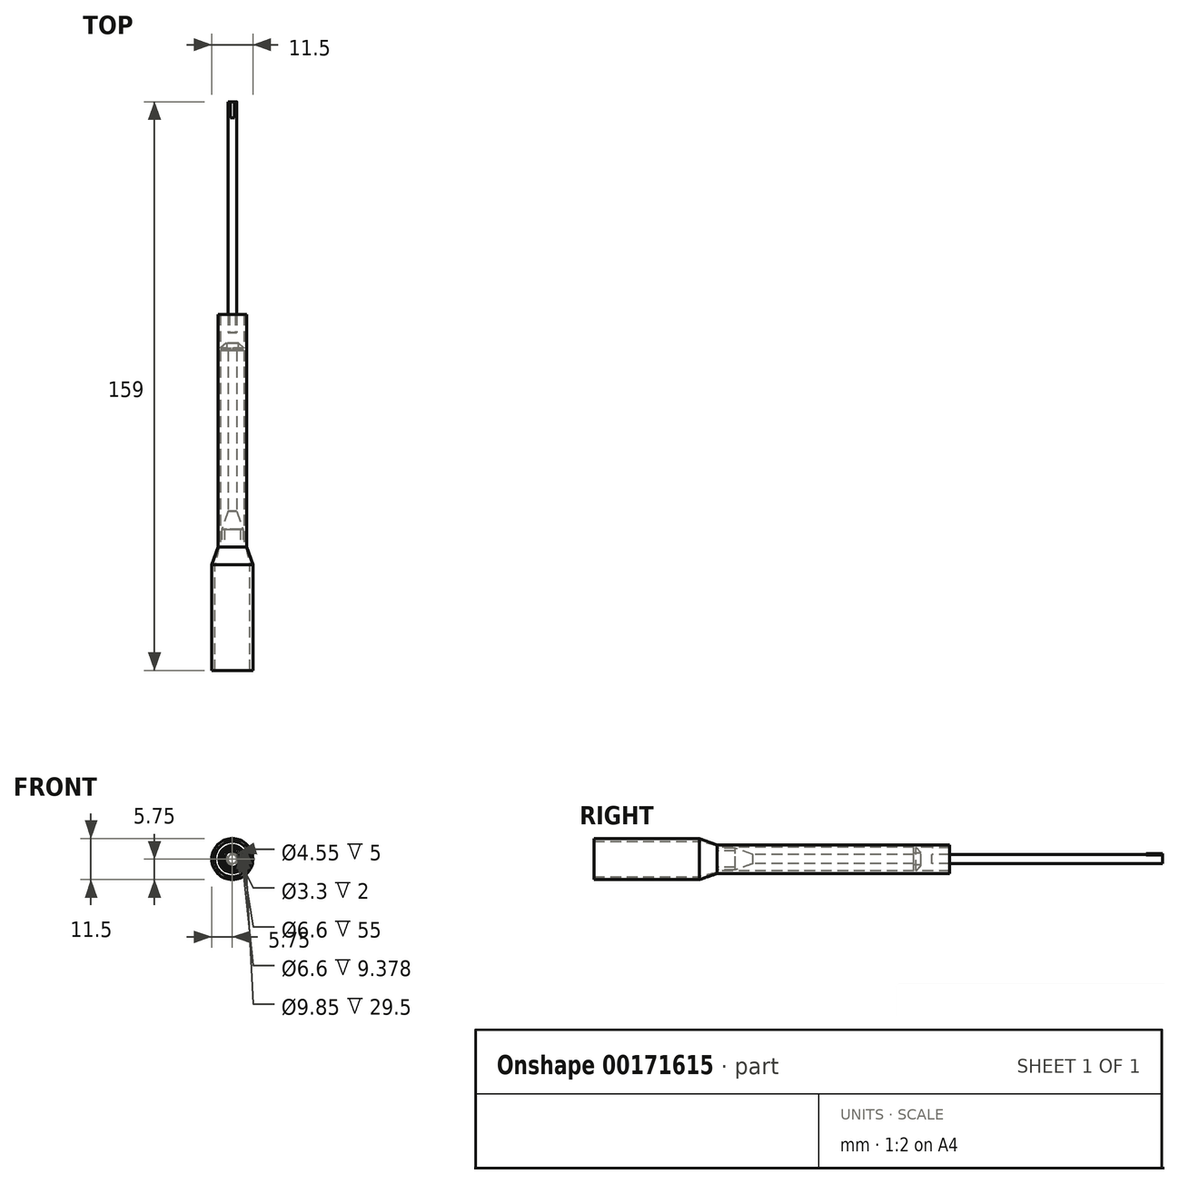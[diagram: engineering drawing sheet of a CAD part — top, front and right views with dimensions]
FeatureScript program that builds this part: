
annotation { "Feature Type Name" : "Feature", "Feature Type Description" : "" }
export const myFeature = defineFeature(function(context is Context, id is Id, definition is map)
    precondition{}
    {
        {
            var Q0;
            Q0=qCreatedBy(makeId("Front.planeOp"),FACE);
            var sketch = newSketch(context, id + "F0", { "sketchPlane" : qUnion([Q0])});
            skCircle(sketch, "E0", {"center": v(0, 0) * mm, "radius": 2.27 * mm});
            skCircle(sketch, "E1", {"center": v(0, 0) * mm, "radius": 3 * mm});
            skSolve(sketch);
        }
        {
            var Q0;
            Q0=makeQuery(id+"F0.imprint","IMPRINT",FACE,{"disambiguationData":[TD([[makeQuery(id+"F0.imprint","IMPRINT",EDGE,{"derivedFrom":sQuery(id+"F0.wireOp",EDGE,"E0")}),-1.0]])]});
            extrude(context, id + "F1", {"entities" : qUnion([Q0]), "oppositeDirection" : true, "depth" : 5 * mm});
        }
        {
            var Q0;
            Q0=qCreatedBy(makeId("Front.planeOp"),FACE);
            cPlane(context, id + "F2", {"entities" : qUnion([Q0]), "cplaneType" : CPlaneType.OFFSET, "offset" : 5 * mm, "oppositeDirection" : true, "width" : 150 * mm, "height" : 150 * mm});
        }
        {
            var Q0;
            Q0=qCreatedBy(id+"F2.planeOp",FACE);
            var sketch = newSketch(context, id + "F3", { "sketchPlane" : qUnion([Q0])});
            skCircle(sketch, "E2", {"center": v(0, 0) * mm, "radius": 3 * mm});
            skSolve(sketch);
        }
        {
            var Q0;
            Q0=qCreatedBy(id+"F2.planeOp",FACE);
            cPlane(context, id + "F4", {"entities" : qUnion([Q0]), "cplaneType" : CPlaneType.OFFSET, "offset" : 5 * mm, "oppositeDirection" : true, "width" : 150 * mm, "height" : 150 * mm});
        }
        {
            var Q0;
            Q0=qCreatedBy(id+"F4.planeOp",FACE);
            var sketch = newSketch(context, id + "F5", { "sketchPlane" : qUnion([Q0])});
            skCircle(sketch, "E3", {"center": v(0, 0) * mm, "radius": 1.25 * mm});
            skSolve(sketch);
        }
        {
            var Q1;
            Q1 = qSketchRegion(id + "F5", true);
            var Q2;
            Q2 = qSketchRegion(id + "F3", true);
            loft(context, id + "F6", {"operationType" : NewBodyOperationType.ADD, "sheetProfilesArray" : [{ "sheetProfileEntities" : qUnion([Q1]) }, { "sheetProfileEntities" : qUnion([Q2]) }]});
        }
        {
            var Q0;
            Q0 = qSketchRegion(id + "F5", true);
            extrude(context, id + "F7", {"entities" : qUnion([Q0]), "operationType" : NewBodyOperationType.ADD, "oppositeDirection" : true, "depth" : 110 * mm});
        }
        {
            var Q0;
            Q0=qCreatedBy(id+"F4.planeOp",FACE);
            cPlane(context, id + "F8", {"entities" : qUnion([Q0]), "cplaneType" : CPlaneType.OFFSET, "offset" : 110 * mm, "oppositeDirection" : true, "width" : 150 * mm, "height" : 150 * mm});
        }
        {
            var Q0;
            Q0=qCreatedBy(id+"F8.planeOp",FACE);
            var sketch = newSketch(context, id + "F9", { "sketchPlane" : qUnion([Q0])});
            skArc(sketch, "E4", {"start": v(-0.55, 1.12) * mm, "mid": v(0, -1.25) * mm, "end": v(0.55, 1.12) * mm});
            skLineSegment(sketch, "E5.bottom", {"start": v(-0.55, 1.5) * mm, "end": v(0.55, 1.5) * mm});
            skLineSegment(sketch, "E5.left", {"start": v(-0.55, 1.5) * mm, "end": v(-0.55, 1.12) * mm});
            skLineSegment(sketch, "E5.right", {"start": v(0.55, 1.5) * mm, "end": v(0.55, 1.12) * mm});
            skPoint(sketch, "E5.middle", {"position": v(0, 1.25) * mm});
            skPoint(sketch, "E6", {"position": v(-0.55, 1.12) * mm});
            skPoint(sketch, "E7", {"position": v(0.55, 1.12) * mm});
            skPoint(sketch, "E8.orphan", {"position": v(-0.55, 1) * mm});
            skPoint(sketch, "E9.orphan", {"position": v(0.55, 1) * mm});
            skSolve(sketch);
        }
        {
            var Q0;
            Q0=qCreatedBy(id+"F8.planeOp",FACE);
            cPlane(context, id + "F10", {"entities" : qUnion([Q0]), "cplaneType" : CPlaneType.OFFSET, "offset" : 5 * mm, "oppositeDirection" : true, "width" : 150 * mm, "height" : 150 * mm});
        }
        {
            var Q0;
            Q0=qCreatedBy(id+"F10.planeOp",FACE);
            var sketch = newSketch(context, id + "F11", { "sketchPlane" : qUnion([Q0])});
            skSolve(sketch);
        }
        {
            var Q0;
            Q0 = qSketchRegion(id + "F11", true);
            var Q1;
            Q1 = qSketchRegion(id + "F9", true);
            extrude(context, id + "F12", {"entities" : qUnion([Q0, Q1]), "operationType" : NewBodyOperationType.ADD, "oppositeDirection" : true, "depth" : 4.5 * mm});
        }
        {
            var Q0;
            Q0=qCreatedBy(makeId("Front.planeOp"),FACE);
            var sketch = newSketch(context, id + "F13", { "sketchPlane" : qUnion([Q0])});
            skCircle(sketch, "E10", {"center": v(0, 0) * mm, "radius": 3.3 * mm});
            skCircle(sketch, "E11", {"center": v(0, 0) * mm, "radius": 4 * mm});
            skSolve(sketch);
        }
        {
            var Q0;
            Q0 = qSketchRegion(id + "F13", true);
            extrude(context, id + "F14", {"entities" : qUnion([Q0]), "oppositeDirection" : true, "depth" : 60 * mm});
        }
        {
            var Q0;
            Q0=qCreatedBy(makeId("Front.planeOp"),FACE);
            cPlane(context, id + "F15", {"entities" : qUnion([Q0]), "cplaneType" : CPlaneType.OFFSET, "offset" : 57 * mm, "oppositeDirection" : true, "width" : 150 * mm, "height" : 150 * mm});
        }
        {
            var Q0;
            Q0=qCreatedBy(id+"F15.planeOp",FACE);
            var sketch = newSketch(context, id + "F16", { "sketchPlane" : qUnion([Q0])});
            skCircle(sketch, "E12", {"center": v(0, 0) * mm, "radius": 1.75 * mm});
            skSolve(sketch);
        }
        {
            var Q0;
            Q0=qCreatedBy(makeId("Front.planeOp"),FACE);
            cPlane(context, id + "F17", {"entities" : qUnion([Q0]), "cplaneType" : CPlaneType.OFFSET, "offset" : 55 * mm, "oppositeDirection" : true, "width" : 150 * mm, "height" : 150 * mm});
        }
        {
            var Q0;
            Q0=qCreatedBy(id+"F17.planeOp",FACE);
            var sketch = newSketch(context, id + "F18", { "sketchPlane" : qUnion([Q0])});
            skCircle(sketch, "E13", {"center": v(0, 0) * mm, "radius": 4 * mm});
            skSolve(sketch);
        }
        {
            var Q1;
            Q1 = qSketchRegion(id + "F16", true);
            var Q2;
            Q2 = qSketchRegion(id + "F18", true);
            loft(context, id + "F19", {"operationType" : NewBodyOperationType.ADD, "sheetProfilesArray" : [{ "sheetProfileEntities" : qUnion([Q1]) }, { "sheetProfileEntities" : qUnion([Q2]) }]});
        }
        {
            var Q0;
            Q0=qCreatedBy(id+"F17.planeOp",FACE);
            var sketch = newSketch(context, id + "F20", { "sketchPlane" : qUnion([Q0])});
            skCircle(sketch, "E14", {"center": v(0, 0) * mm, "radius": 1.65 * mm});
            skSolve(sketch);
        }
        {
            var Q0;
            Q0 = qSketchRegion(id + "F20", true);
            extrude(context, id + "F21", {"entities" : qUnion([Q0]), "operationType" : NewBodyOperationType.REMOVE, "oppositeDirection" : true, "depth" : 5 * mm});
        }
        {
            var Q0;
            Q0=qCreatedBy(id+"F15.planeOp",FACE);
            cPlane(context, id + "F22", {"entities" : qUnion([Q0]), "cplaneType" : CPlaneType.OFFSET, "offset" : 3 * mm, "oppositeDirection" : true, "width" : 150 * mm, "height" : 150 * mm});
        }
        {
            var Q0;
            Q0=qCreatedBy(id+"F22.planeOp",FACE);
            var sketch = newSketch(context, id + "F23", { "sketchPlane" : qUnion([Q0])});
            skArc(sketch, "E15", {"start": v(-0.83, 3.2) * mm, "mid": v(0, -3.3) * mm, "end": v(0.83, 3.2) * mm});
            skCircle(sketch, "E16", {"center": v(0, 0) * mm, "radius": 4 * mm});
            skLineSegment(sketch, "E17.bottom", {"start": v(0.83, 3.65) * mm, "end": v(-0.82, 3.65) * mm});
            skLineSegment(sketch, "E17.left", {"start": v(0.82, 3.65) * mm, "end": v(0.82, 3.2) * mm});
            skLineSegment(sketch, "E17.right", {"start": v(-0.82, 3.65) * mm, "end": v(-0.82, 3.2) * mm});
            skPoint(sketch, "E17.middle", {"position": v(0, 3.3) * mm});
            skPoint(sketch, "E18", {"position": v(0.82, 3.2) * mm});
            skPoint(sketch, "E19", {"position": v(-0.82, 3.2) * mm});
            skPoint(sketch, "E20.orphan", {"position": v(0.82, 2.95) * mm});
            skPoint(sketch, "E21.orphan", {"position": v(-0.82, 2.95) * mm});
            skSolve(sketch);
        }
        {
            var Q0;
            Q0 = qSketchRegion(id + "F23", true);
            extrude(context, id + "F24", {"entities" : qUnion([Q0]), "operationType" : NewBodyOperationType.ADD, "oppositeDirection" : true, "depth" : 5 * mm});
        }
        {
            var Q0;
            Q0=qCreatedBy(id+"F22.planeOp",FACE);
            cPlane(context, id + "F25", {"entities" : qUnion([Q0]), "cplaneType" : CPlaneType.OFFSET, "offset" : 5 * mm, "oppositeDirection" : true, "width" : 150 * mm, "height" : 150 * mm});
        }
        {
            var Q0;
            Q0=qCreatedBy(makeId("Front.planeOp"),FACE);
            cPlane(context, id + "F26", {"entities" : qUnion([Q0]), "cplaneType" : CPlaneType.OFFSET, "offset" : 5 * mm, "width" : 150 * mm, "height" : 150 * mm});
        }
        {
            var Q0;
            Q0=qCreatedBy(id+"F26.planeOp",FACE);
            var sketch = newSketch(context, id + "F27", { "sketchPlane" : qUnion([Q0])});
            skCircle(sketch, "E22", {"center": v(0, 0) * mm, "radius": 5.75 * mm});
            skSolve(sketch);
        }
        {
            var Q0;
            Q0=qCreatedBy(makeId("Front.planeOp"),FACE);
            var sketch = newSketch(context, id + "F28", { "sketchPlane" : qUnion([Q0])});
            skCircle(sketch, "E23", {"center": v(0, 0) * mm, "radius": 4 * mm});
            skSolve(sketch);
        }
        {
            var Q1;
            Q1 = qSketchRegion(id + "F28", true);
            var Q2;
            Q2 = qSketchRegion(id + "F27", true);
            loft(context, id + "F29", {"operationType" : NewBodyOperationType.ADD, "sheetProfilesArray" : [{ "sheetProfileEntities" : qUnion([Q1]) }, { "sheetProfileEntities" : qUnion([Q2]) }]});
        }
        {
            var Q0;
            Q0=qCreatedBy(makeId("Front.planeOp"),FACE);
            var sketch = newSketch(context, id + "F30", { "sketchPlane" : qUnion([Q0])});
            skCircle(sketch, "E24", {"center": v(0, 0) * mm, "radius": 3.75 * mm});
            skSolve(sketch);
        }
        {
            var Q0;
            Q0=qCreatedBy(id+"F26.planeOp",FACE);
            var sketch = newSketch(context, id + "F31", { "sketchPlane" : qUnion([Q0])});
            skCircle(sketch, "E25", {"center": v(0, 0) * mm, "radius": 4.92 * mm});
            skSolve(sketch);
        }
        {
            var Q1;
            Q1 = qSketchRegion(id + "F30", true);
            var Q2;
            Q2 = qSketchRegion(id + "F31", true);
            loft(context, id + "F32", {"operationType" : NewBodyOperationType.REMOVE, "sheetProfilesArray" : [{ "sheetProfileEntities" : qUnion([Q1]) }, { "sheetProfileEntities" : qUnion([Q2]) }]});
        }
        {
            var Q0;
            Q0 = qSketchRegion(id + "F27", true);
            extrude(context, id + "F33", {"entities" : qUnion([Q0]), "operationType" : NewBodyOperationType.ADD, "depth" : 29.5 * mm});
        }
        {
            var Q0;
            Q0 = qSketchRegion(id + "F31", true);
            extrude(context, id + "F34", {"entities" : qUnion([Q0]), "operationType" : NewBodyOperationType.REMOVE, "depth" : 29.6 * mm});
        }
    });
